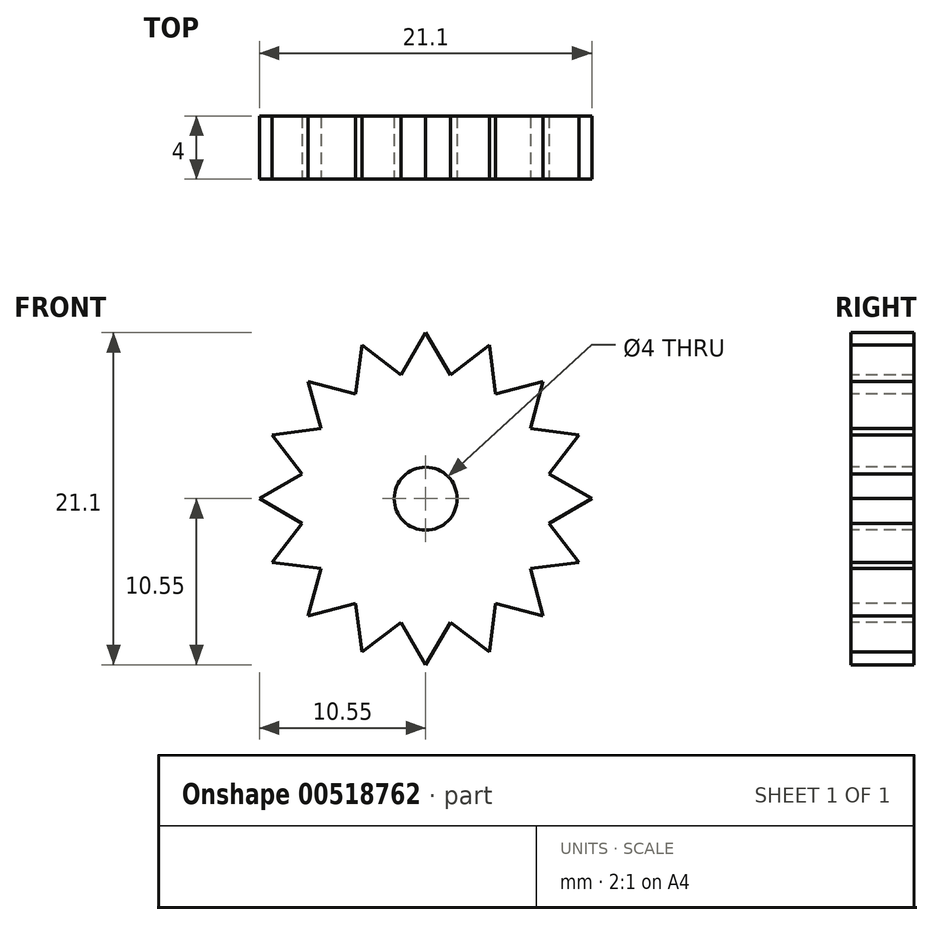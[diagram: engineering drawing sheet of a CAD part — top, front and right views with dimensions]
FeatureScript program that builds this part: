
annotation { "Feature Type Name" : "Feature", "Feature Type Description" : "" }
export const myFeature = defineFeature(function(context is Context, id is Id, definition is map)
    precondition{}
    {
        {
            var Q0;
            Q0=qCreatedBy(makeId("Front.planeOp"),FACE);
            var sketch = newSketch(context, id + "F0", { "sketchPlane" : qUnion([Q0])});
            skCircle(sketch, "E0", {"center": v(0, 0) * mm, "radius": 8 * mm});
            skLineSegment(sketch, "E1", {"start": v(0, 10.55) * mm, "end": v(-1.56, 7.85) * mm});
            skCircle(sketch, "E2", {"center": v(0, 0) * mm, "radius": 2 * mm});
            skLineSegment(sketch, "E3", {"start": v(0, 0) * mm, "end": v(-1.56, 7.85) * mm, "construction": true});
            skLineSegment(sketch, "E4", {"start": v(0, 10.55) * mm, "end": v(1.56, 7.85) * mm});
            skLineSegment(sketch, "E5.1.0", {"start": v(-4.04, 9.75) * mm, "end": v(-4.44, 6.65) * mm});
            skLineSegment(sketch, "E5.1.1", {"start": v(-4.04, 9.75) * mm, "end": v(-1.56, 7.85) * mm});
            skLineSegment(sketch, "E5.2.0", {"start": v(-7.46, 7.46) * mm, "end": v(-6.65, 4.44) * mm});
            skLineSegment(sketch, "E5.2.1", {"start": v(-7.46, 7.46) * mm, "end": v(-4.44, 6.65) * mm});
            skLineSegment(sketch, "E5.3.0", {"start": v(-9.75, 4.04) * mm, "end": v(-7.85, 1.56) * mm});
            skLineSegment(sketch, "E5.3.1", {"start": v(-9.75, 4.04) * mm, "end": v(-6.65, 4.44) * mm});
            skLineSegment(sketch, "E5.4.0", {"start": v(-10.55, 0) * mm, "end": v(-7.85, -1.56) * mm});
            skLineSegment(sketch, "E5.4.1", {"start": v(-10.55, 0) * mm, "end": v(-7.85, 1.56) * mm});
            skLineSegment(sketch, "E5.5.0", {"start": v(-9.75, -4.04) * mm, "end": v(-6.65, -4.44) * mm});
            skLineSegment(sketch, "E5.5.1", {"start": v(-9.75, -4.04) * mm, "end": v(-7.85, -1.56) * mm});
            skLineSegment(sketch, "E5.6.0", {"start": v(-7.46, -7.46) * mm, "end": v(-4.44, -6.65) * mm});
            skLineSegment(sketch, "E5.6.1", {"start": v(-7.46, -7.46) * mm, "end": v(-6.65, -4.44) * mm});
            skLineSegment(sketch, "E5.7.0", {"start": v(-4.04, -9.75) * mm, "end": v(-1.56, -7.85) * mm});
            skLineSegment(sketch, "E5.7.1", {"start": v(-4.04, -9.75) * mm, "end": v(-4.44, -6.65) * mm});
            skLineSegment(sketch, "E5.8.0", {"start": v(0, -10.55) * mm, "end": v(1.56, -7.85) * mm});
            skLineSegment(sketch, "E5.8.1", {"start": v(0, -10.55) * mm, "end": v(-1.56, -7.85) * mm});
            skLineSegment(sketch, "E5.9.0", {"start": v(4.04, -9.75) * mm, "end": v(4.44, -6.65) * mm});
            skLineSegment(sketch, "E5.9.1", {"start": v(4.04, -9.75) * mm, "end": v(1.56, -7.85) * mm});
            skLineSegment(sketch, "E5.10.0", {"start": v(7.46, -7.46) * mm, "end": v(6.65, -4.44) * mm});
            skLineSegment(sketch, "E5.10.1", {"start": v(7.46, -7.46) * mm, "end": v(4.44, -6.65) * mm});
            skLineSegment(sketch, "E5.11.0", {"start": v(9.75, -4.04) * mm, "end": v(7.85, -1.56) * mm});
            skLineSegment(sketch, "E5.11.1", {"start": v(9.75, -4.04) * mm, "end": v(6.65, -4.44) * mm});
            skLineSegment(sketch, "E5.12.0", {"start": v(10.55, 0) * mm, "end": v(7.85, 1.56) * mm});
            skLineSegment(sketch, "E5.12.1", {"start": v(10.55, 0) * mm, "end": v(7.85, -1.56) * mm});
            skLineSegment(sketch, "E5.13.0", {"start": v(9.75, 4.04) * mm, "end": v(6.65, 4.44) * mm});
            skLineSegment(sketch, "E5.13.1", {"start": v(9.75, 4.04) * mm, "end": v(7.85, 1.56) * mm});
            skLineSegment(sketch, "E5.14.0", {"start": v(7.46, 7.46) * mm, "end": v(4.44, 6.65) * mm});
            skLineSegment(sketch, "E5.14.1", {"start": v(7.46, 7.46) * mm, "end": v(6.65, 4.44) * mm});
            skLineSegment(sketch, "E5.15.0", {"start": v(4.04, 9.75) * mm, "end": v(1.56, 7.85) * mm});
            skLineSegment(sketch, "E5.15.1", {"start": v(4.04, 9.75) * mm, "end": v(4.44, 6.65) * mm});
            skSolve(sketch);
        }
        {
            var Q0;
            Q0 = qSketchRegion(id + "F0", true);
            extrude(context, id + "F1", {"entities" : qUnion([Q0]), "endBound" : BoundingType.SYMMETRIC, "oppositeDirection" : true, "depth" : 4 * mm, "offsetDistance" : 25 * mm});
        }
    });
